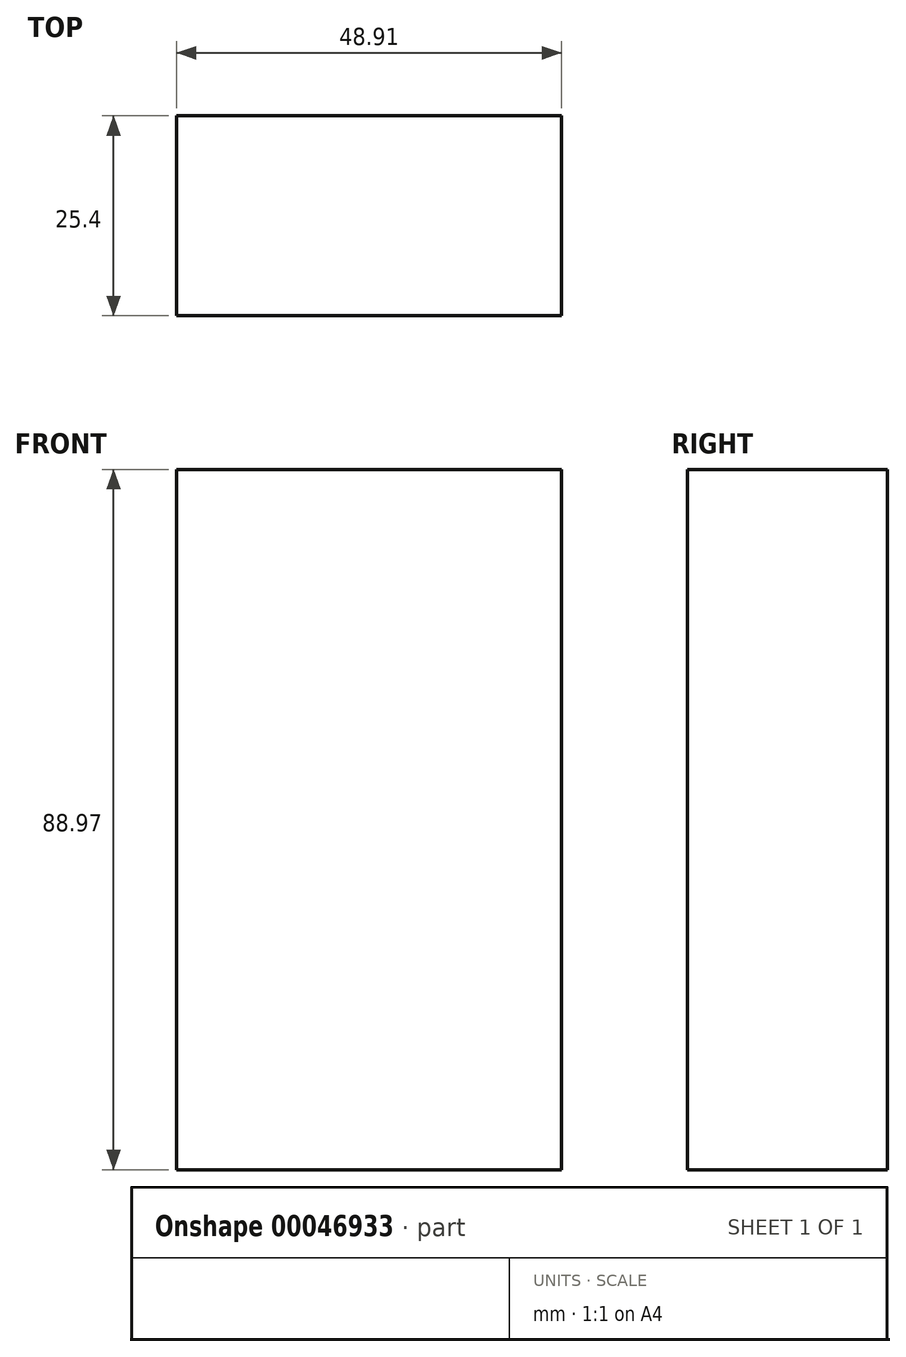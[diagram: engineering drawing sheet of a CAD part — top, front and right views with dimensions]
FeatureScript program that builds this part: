
annotation { "Feature Type Name" : "Feature", "Feature Type Description" : "" }
export const myFeature = defineFeature(function(context is Context, id is Id, definition is map)
    precondition{}
    {
        {
            var Q0;
            Q0=qCreatedBy(makeId("Front.planeOp"),FACE);
            var sketch = newSketch(context, id + "F0", { "sketchPlane" : qUnion([Q0])});
            skLineSegment(sketch, "E0.bottom", {"start": v(-24.34, 44.83) * mm, "end": v(24.57, 44.83) * mm});
            skLineSegment(sketch, "E0.top", {"start": v(-24.34, -44.14) * mm, "end": v(24.57, -44.14) * mm});
            skLineSegment(sketch, "E0.left", {"start": v(-24.34, 44.83) * mm, "end": v(-24.34, -44.14) * mm});
            skLineSegment(sketch, "E0.right", {"start": v(24.57, 44.83) * mm, "end": v(24.57, -44.14) * mm});
            skSolve(sketch);
        }
        {
            var Q0;
            Q0=makeQuery(id+"F0.imprint","IMPRINT",FACE,{"disambiguationData":[TD([[makeQuery(id+"F0.imprint","IMPRINT",EDGE,{"derivedFrom":sQuery(id+"F0.wireOp",EDGE,"E0.bottom")}),-1.0]])]});
            extrude(context, id + "F1", {"entities" : qUnion([Q0]), "depth" : 25.4 * mm});
        }
    });
